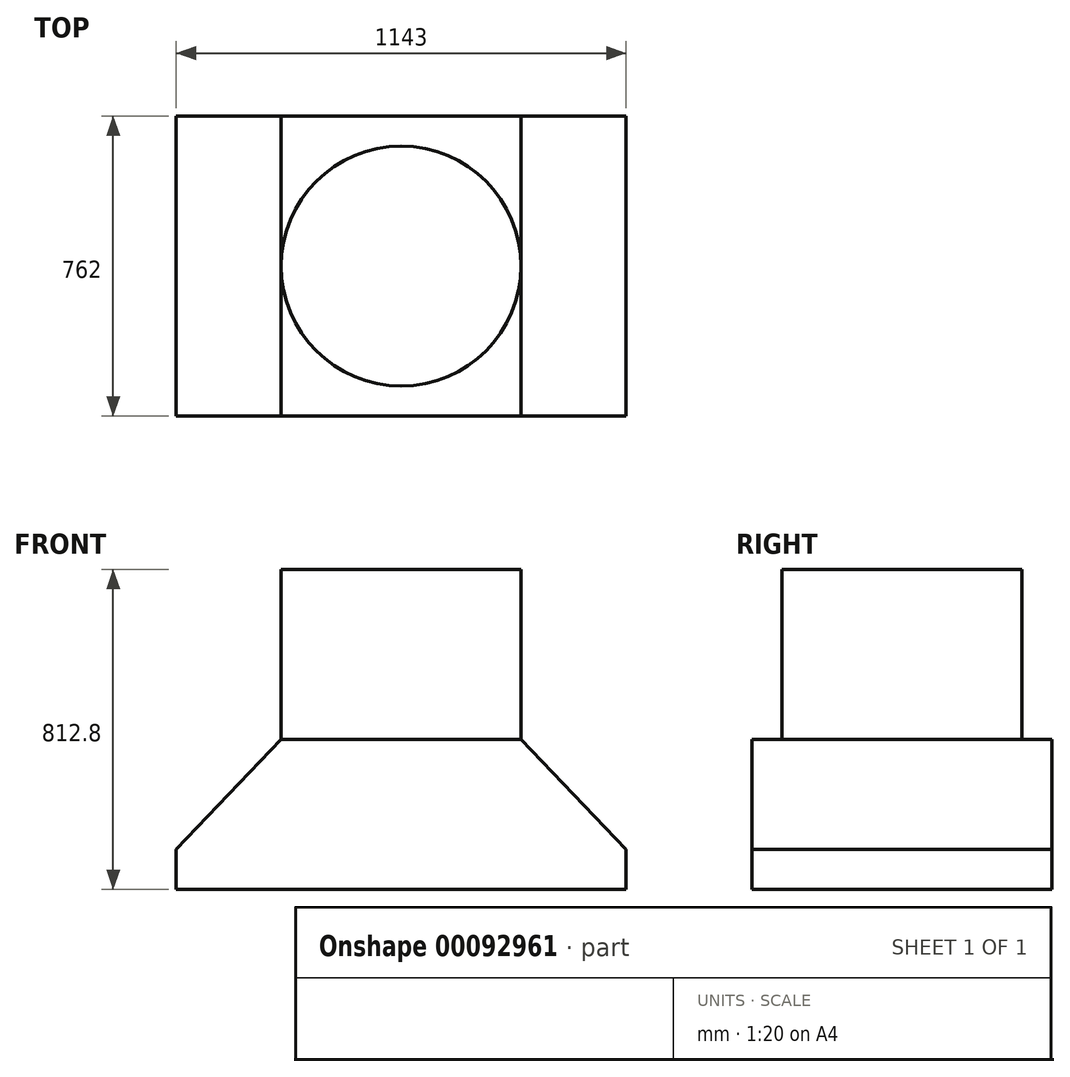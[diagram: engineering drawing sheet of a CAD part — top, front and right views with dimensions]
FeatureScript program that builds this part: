
annotation { "Feature Type Name" : "Feature", "Feature Type Description" : "" }
export const myFeature = defineFeature(function(context is Context, id is Id, definition is map)
    precondition{}
    {
        {
            var Q0;
            Q0=qCreatedBy(makeId("Front.planeOp"),FACE);
            var sketch = newSketch(context, id + "F0", { "sketchPlane" : qUnion([Q0])});
            skLineSegment(sketch, "E0.bottom", {"start": v(304.8, 190.5) * mm, "end": v(-304.8, 190.5) * mm});
            skLineSegment(sketch, "E0.top", {"start": v(571.5, -190.5) * mm, "end": v(-571.5, -190.5) * mm});
            skLineSegment(sketch, "E0.left", {"start": v(571.5, -88.9) * mm, "end": v(571.5, -190.5) * mm});
            skLineSegment(sketch, "E0.right", {"start": v(-571.5, -88.9) * mm, "end": v(-571.5, -190.5) * mm});
            skPoint(sketch, "E0.middle", {"position": v(0, 0) * mm});
            skLineSegment(sketch, "E1", {"start": v(-571.5, -88.9) * mm, "end": v(-304.8, 190.5) * mm});
            skLineSegment(sketch, "E2", {"start": v(304.8, 190.5) * mm, "end": v(571.5, -88.9) * mm});
            skPoint(sketch, "E3.orphan", {"position": v(571.5, 190.5) * mm});
            skPoint(sketch, "E4.orphan", {"position": v(-571.5, 190.5) * mm});
            skSolve(sketch);
        }
        {
            var Q0;
            Q0 = qSketchRegion(id + "F0", true);
            extrude(context, id + "F1", {"entities" : qUnion([Q0]), "depth" : 25.4 * mm});
        }
        {
            var Q0;
            Q0 = qSketchRegion(id + "F0", true);
            extrude(context, id + "F2", {"entities" : qUnion([Q0]), "operationType" : NewBodyOperationType.ADD, "depth" : 762 * mm});
        }
        {
            var Q0;
            {var subQ0=sQuery(id+"F0.wireOp",EDGE,"E0.bottom");Q0=makeQuery(id+"F2.boolean.opBoolean","MERGE",FACE,{"derivedFrom":[makeQuery(id+"F1.opExtrude","SWEPT_FACE",FACE,{"disambiguationData":[OSD([subQ0])]}),makeQuery(id+"F2.opExtrude","SWEPT_FACE",FACE,{"disambiguationData":[OSD([subQ0])]})]});}
            var sketch = newSketch(context, id + "F3", { "sketchPlane" : qUnion([Q0])});
            skCircle(sketch, "E5", {"center": v(0, -381) * mm, "radius": 304.8 * mm});
            skPoint(sketch, "E5.centerSnap0", {"position": v(-304.8, -381) * mm});
            skPoint(sketch, "E5.centerSnap1", {"position": v(0, 0) * mm});
            skSolve(sketch);
        }
        {
            var Q0;
            Q0 = qSketchRegion(id + "F3", true);
            var Q1;
            {var subQ0=sQuery(id+"F3.wireOp",EDGE,"E5");var subQ1=sQuery(id+"F0.wireOp",EDGE,"E2");var subQ2=sQuery(id+"F0.wireOp",EDGE,"E0.bottom");var subQ3=makeQuery(id+"F3.imprint","INTERSECT",VERTEX,{"derivedFrom":[makeQuery(id+"F2.boolean.opBoolean","MERGE",EDGE,{"derivedFrom":[makeQuery(id+"F1.opExtrude","SWEPT_EDGE",EDGE,{"disambiguationData":[OSD([subQ2,subQ1])]}),makeQuery(id+"F2.opExtrude","SWEPT_EDGE",EDGE,{"disambiguationData":[OSD([subQ2,subQ1])]})]}),subQ0]});Q1=makeQuery(id+"F3.imprint","IMPRINT",FACE,{"disambiguationData":[TD([[makeQuery(id+"F3.imprint","IMPRINT",EDGE,{"disambiguationData":[TD([[subQ3,-1.0]])],"derivedFrom":subQ0}),1.0]])]});}
            extrude(context, id + "F4", {"entities" : qUnion([Q0, Q1]), "operationType" : NewBodyOperationType.ADD, "depth" : 431.8 * mm});
        }
    });
